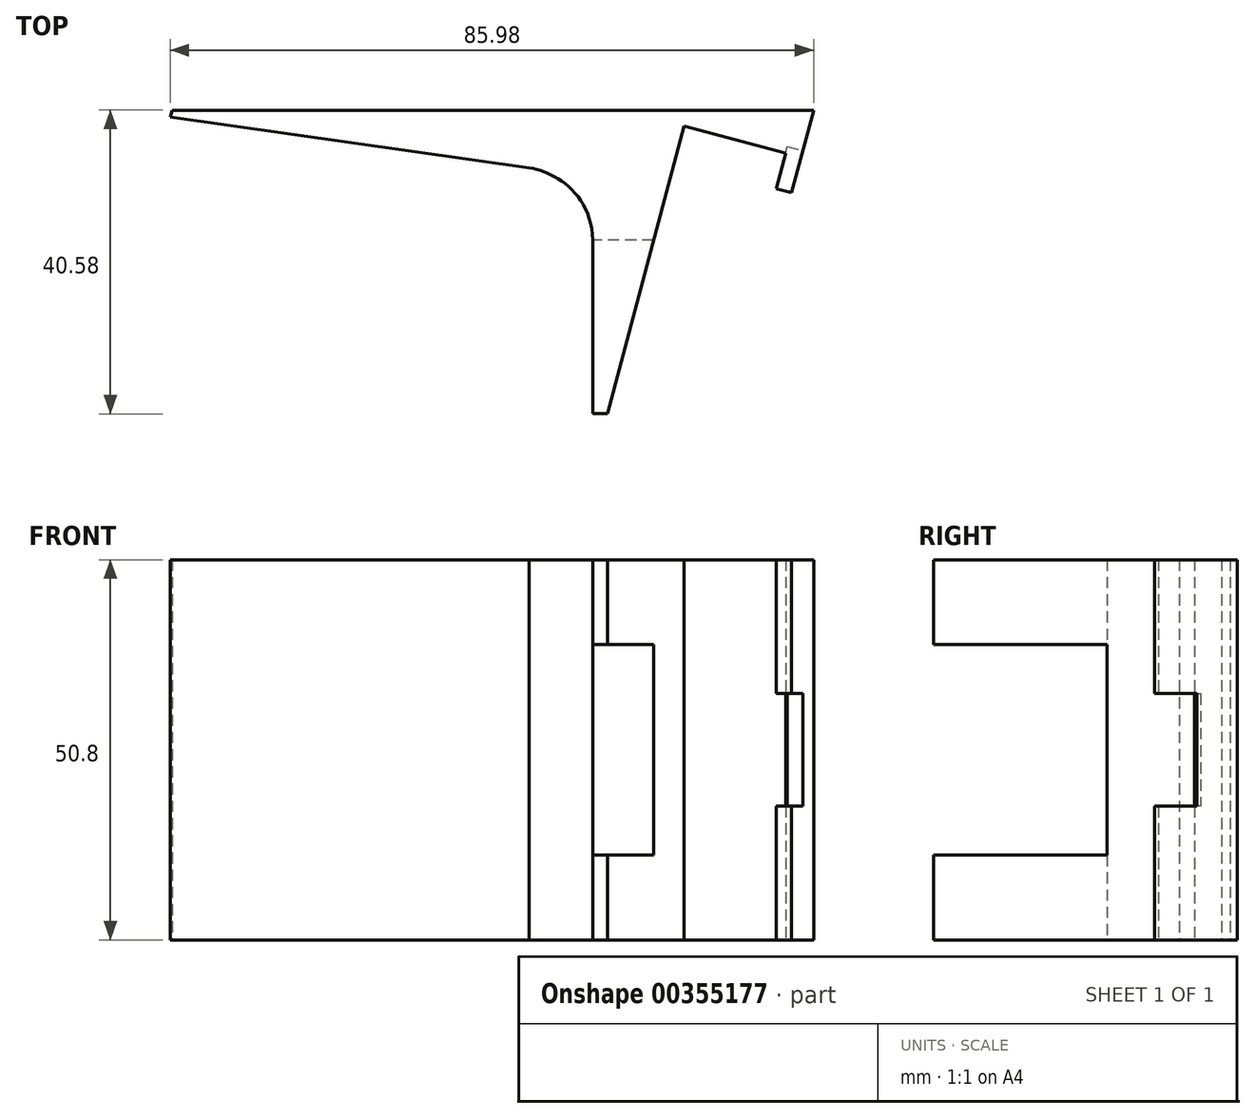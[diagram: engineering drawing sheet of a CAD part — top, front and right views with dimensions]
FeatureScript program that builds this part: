
annotation { "Feature Type Name" : "Feature", "Feature Type Description" : "" }
export const myFeature = defineFeature(function(context is Context, id is Id, definition is map)
    precondition{}
    {
        {
            var Q0;
            Q0=qCreatedBy(makeId("Top.planeOp"),FACE);
            var sketch = newSketch(context, id + "F0", { "sketchPlane" : qUnion([Q0])});
            skLineSegment(sketch, "E0", {"start": v(42.83, 20.29) * mm, "end": v(39.89, 9.24) * mm});
            skLineSegment(sketch, "E1", {"start": v(39.89, 9.24) * mm, "end": v(37.8, 9.8) * mm});
            skLineSegment(sketch, "E2", {"start": v(37.8, 9.8) * mm, "end": v(39.07, 14.57) * mm});
            skLineSegment(sketch, "E3", {"start": v(39.07, 14.57) * mm, "end": v(25.5, 18.18) * mm});
            skLineSegment(sketch, "E4", {"start": v(25.5, 18.18) * mm, "end": v(15.26, -20.29) * mm});
            skLineSegment(sketch, "E5", {"start": v(15.26, -20.29) * mm, "end": v(13.34, -20.29) * mm});
            skLineSegment(sketch, "E6", {"start": v(13.34, -20.29) * mm, "end": v(13.34, 2.9) * mm});
            skLineSegment(sketch, "E7", {"start": v(42.83, 20.29) * mm, "end": v(-42.9, 20.29) * mm});
            skLineSegment(sketch, "E8", {"start": v(-42.9, 20.29) * mm, "end": v(-43.15, 19.34) * mm});
            skLineSegment(sketch, "E9", {"start": v(-43.15, 19.34) * mm, "end": v(4.83, 12.59) * mm});
            skFitSpline(sketch, "E10", {"points": [v(4.83, 12.59) * mm, v(13.34, 2.9) * mm], "startDerivative": vector(10.64, -1.82) * mm, "endDerivative": vector(0.82, -18.85) * mm});
            skSolve(sketch);
        }
        {
            var Q0;
            Q0 = qSketchRegion(id + "F0", true);
            extrude(context, id + "F1", {"entities" : qUnion([Q0]), "depth" : 25.4 * mm, "hasSecondDirection" : true, "secondDirectionOppositeDirection" : true, "secondDirectionDepth" : 25.4 * mm});
        }
        {
            var Q0;
            Q0=makeQuery(id+"F1.opExtrude","SWEPT_FACE",FACE,{"disambiguationData":[OSD([sQuery(id+"F0.wireOp",EDGE,"E0")])]});
            var sketch = newSketch(context, id + "F2", { "sketchPlane" : qUnion([Q0])});
            skLineSegment(sketch, "E11", {"start": v(19.19, -7.53) * mm, "end": v(19.19, 7.5) * mm});
            skLineSegment(sketch, "E12", {"start": v(19.19, 7.5) * mm, "end": v(25.03, 7.5) * mm});
            skLineSegment(sketch, "E13", {"start": v(25.03, 7.5) * mm, "end": v(25.03, -7.53) * mm});
            skLineSegment(sketch, "E14", {"start": v(25.03, -7.53) * mm, "end": v(19.19, -7.53) * mm});
            skSolve(sketch);
        }
        {
            var Q0;
            Q0=makeQuery(id+"F2.imprint","IMPRINT",FACE,{"disambiguationData":[TD([[makeQuery(id+"F2.imprint","IMPRINT",EDGE,{"derivedFrom":sQuery(id+"F2.wireOp",EDGE,"E11")}),1.0]])]});
            var Q1;
            Q1=makeQuery(id+"F1.opExtrude","SWEPT_FACE",FACE,{"disambiguationData":[OSD([sQuery(id+"F0.wireOp",EDGE,"E2")])]});
            extrude(context, id + "F3", {"entities" : qUnion([Q0]), "operationType" : NewBodyOperationType.REMOVE, "endBound" : BoundingType.UP_TO_SURFACE, "oppositeDirection" : true, "endBoundEntityFace" : qUnion([Q1]), "depth" : 25.4 * mm});
        }
        {
            var Q0;
            Q0=makeQuery(id+"F1.opExtrude","SWEPT_FACE",FACE,{"disambiguationData":[OSD([sQuery(id+"F0.wireOp",EDGE,"E6")])]});
            var sketch = newSketch(context, id + "F4", { "sketchPlane" : qUnion([Q0])});
            skLineSegment(sketch, "E15.bottom", {"start": v(20.29, 14.1) * mm, "end": v(-2.9, 14.1) * mm});
            skLineSegment(sketch, "E15.top", {"start": v(20.29, -14.07) * mm, "end": v(-2.9, -14.07) * mm});
            skLineSegment(sketch, "E15.left", {"start": v(20.29, 14.1) * mm, "end": v(20.29, -14.07) * mm});
            skLineSegment(sketch, "E15.right", {"start": v(-2.9, 14.1) * mm, "end": v(-2.9, -14.07) * mm});
            skSolve(sketch);
        }
        {
            var Q0;
            Q0 = qSketchRegion(id + "F4", true);
            extrude(context, id + "F5", {"entities" : qUnion([Q0]), "operationType" : NewBodyOperationType.REMOVE, "endBound" : BoundingType.UP_TO_NEXT, "oppositeDirection" : true, "depth" : 25.4 * mm});
        }
    });
